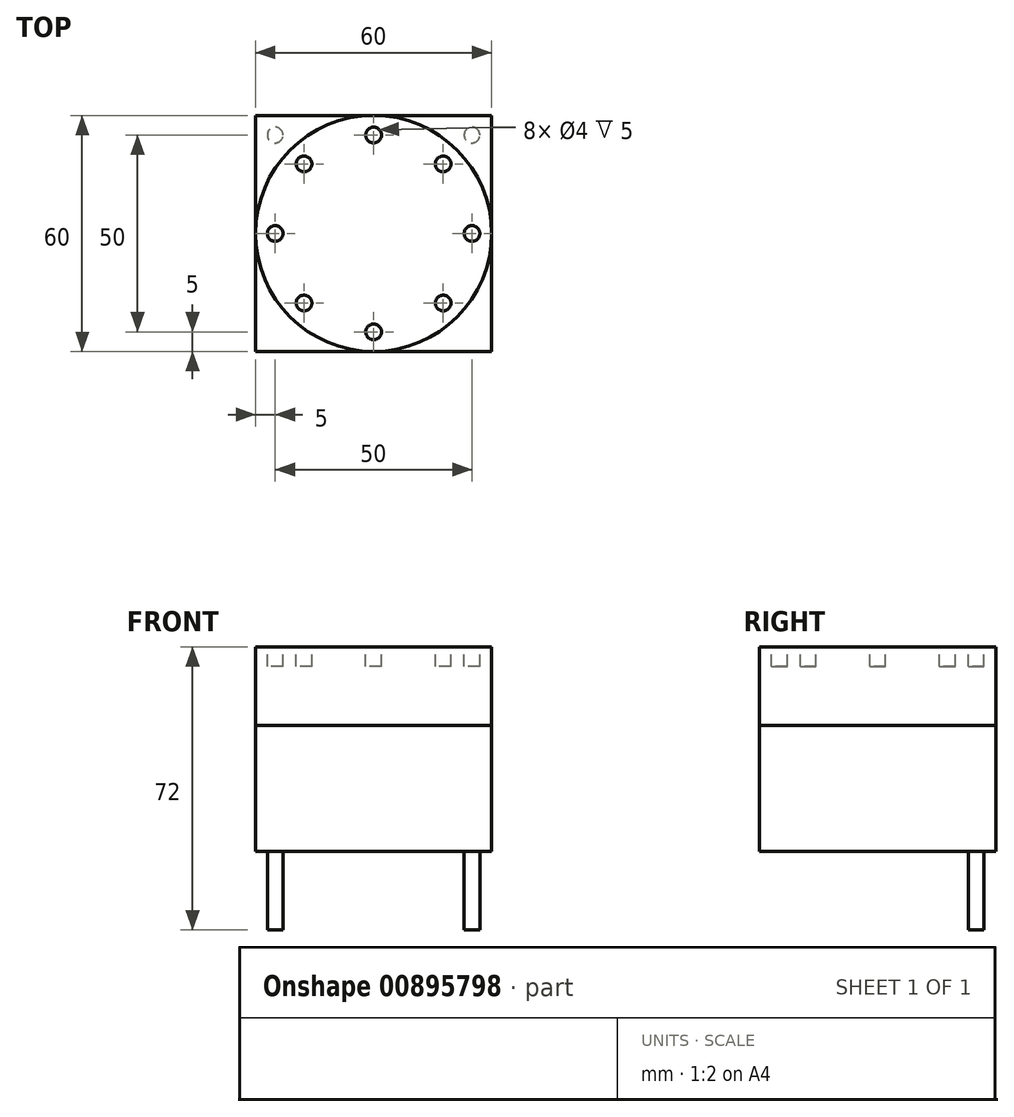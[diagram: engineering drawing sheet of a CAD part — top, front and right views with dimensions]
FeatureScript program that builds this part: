
annotation { "Feature Type Name" : "Feature", "Feature Type Description" : "" }
export const myFeature = defineFeature(function(context is Context, id is Id, definition is map)
    precondition{}
    {
        {
            var Q0;
            Q0=qCreatedBy(makeId("Top.planeOp"),FACE);
            var sketch = newSketch(context, id + "F0", { "sketchPlane" : qUnion([Q0])});
            skLineSegment(sketch, "E0.bottom", {"start": v(-30, 30) * mm, "end": v(30, 30) * mm});
            skLineSegment(sketch, "E0.top", {"start": v(-30, -30) * mm, "end": v(30, -30) * mm});
            skLineSegment(sketch, "E0.left", {"start": v(-30, 30) * mm, "end": v(-30, -30) * mm});
            skLineSegment(sketch, "E0.right", {"start": v(30, 30) * mm, "end": v(30, -30) * mm});
            skPoint(sketch, "E0.middle", {"position": v(0, 0) * mm});
            skCircle(sketch, "E1", {"center": v(0, 0) * mm, "radius": 30 * mm});
            skSolve(sketch);
        }
        {
            var Q0;
            Q0 = qSketchRegion(id + "F0", true);
            extrude(context, id + "F1", {"entities" : qUnion([Q0]), "oppositeDirection" : true, "depth" : 52 * mm, "offsetDistance" : 25 * mm});
        }
        {
            var Q0;
            {var subQ0=sQuery(id+"F0.wireOp",EDGE,"E1");var subQ1=makeQuery(id+"F0.imprint","INTERSECT",VERTEX,{"derivedFrom":[sQuery(id+"F0.wireOp",EDGE,"E0.bottom"),subQ0]});Q0=makeQuery(id+"F0.imprint","IMPRINT",FACE,{"disambiguationData":[TD([[makeQuery(id+"F0.imprint","IMPRINT",EDGE,{"disambiguationData":[TD([[subQ1,1.0]])],"derivedFrom":subQ0}),1.0]])]});}
            extrude(context, id + "F2", {"entities" : qUnion([Q0]), "operationType" : NewBodyOperationType.ADD, "depth" : 20 * mm, "offsetDistance" : 25 * mm});
        }
        {
            var Q0;
            Q0=makeQuery(id+"F2.opExtrude","CAP_FACE",FACE,{"disambiguationData":[OSD([sQuery(id+"F0.wireOp",EDGE,"E1")])],"isStart":false});
            var sketch = newSketch(context, id + "F3", { "sketchPlane" : qUnion([Q0])});
            skCircle(sketch, "E2", {"center": v(0, 25) * mm, "radius": 2 * mm});
            skCircle(sketch, "E3.1.0", {"center": v(-17.68, 17.68) * mm, "radius": 2 * mm});
            skCircle(sketch, "E3.2.0", {"center": v(-25, 0) * mm, "radius": 2 * mm});
            skCircle(sketch, "E3.3.0", {"center": v(-17.68, -17.68) * mm, "radius": 2 * mm});
            skCircle(sketch, "E3.4.0", {"center": v(0, -25) * mm, "radius": 2 * mm});
            skCircle(sketch, "E3.5.0", {"center": v(17.68, -17.68) * mm, "radius": 2 * mm});
            skCircle(sketch, "E3.6.0", {"center": v(25, 0) * mm, "radius": 2 * mm});
            skCircle(sketch, "E3.7.0", {"center": v(17.68, 17.68) * mm, "radius": 2 * mm});
            skPoint(sketch, "E3.center", {"position": v(0, 0) * mm});
            skSolve(sketch);
        }
        {
            var Q0;
            Q0 = qSketchRegion(id + "F3", true);
            extrude(context, id + "F4", {"entities" : qUnion([Q0]), "operationType" : NewBodyOperationType.REMOVE, "oppositeDirection" : true, "depth" : 5 * mm, "offsetDistance" : 25 * mm});
        }
        {
            var Q0;
            Q0=makeQuery(id+"F1.opExtrude","CAP_FACE",FACE,{"disambiguationData":[OSD([sQuery(id+"F0.wireOp",EDGE,"E0.bottom"),sQuery(id+"F0.wireOp",EDGE,"E0.top"),sQuery(id+"F0.wireOp",EDGE,"E0.left"),sQuery(id+"F0.wireOp",EDGE,"E0.right")])],"isStart":false});
            var sketch = newSketch(context, id + "F5", { "sketchPlane" : qUnion([Q0])});
            skCircle(sketch, "E4", {"center": v(-25, 25) * mm, "radius": 2 * mm});
            skCircle(sketch, "E5", {"center": v(25, 25) * mm, "radius": 2 * mm});
            skCircle(sketch, "E6.MirrorC", {"center": v(25, -25) * mm, "radius": 2 * mm});
            skCircle(sketch, "E7.MirrorC", {"center": v(-25, -25) * mm, "radius": 2 * mm});
            skSolve(sketch);
        }
        {
            var Q0;
            Q0=makeQuery(id+"F5.imprint","IMPRINT",FACE,{"disambiguationData":[TD([[makeQuery(id+"F5.imprint","IMPRINT",EDGE,{"derivedFrom":sQuery(id+"F5.wireOp",EDGE,"E4")}),1.0]])]});
            var Q1;
            Q1=makeQuery(id+"F5.imprint","IMPRINT",FACE,{"disambiguationData":[TD([[makeQuery(id+"F5.imprint","IMPRINT",EDGE,{"derivedFrom":sQuery(id+"F5.wireOp",EDGE,"E6.MirrorC")}),-1.0]])]});
            var Q2;
            Q2=makeQuery(id+"F5.imprint","IMPRINT",FACE,{"disambiguationData":[TD([[makeQuery(id+"F5.imprint","IMPRINT",EDGE,{"derivedFrom":sQuery(id+"F5.wireOp",EDGE,"E5")}),1.0]])]});
            var Q3;
            Q3=makeQuery(id+"F5.imprint","IMPRINT",FACE,{"disambiguationData":[TD([[makeQuery(id+"F5.imprint","IMPRINT",EDGE,{"derivedFrom":sQuery(id+"F5.wireOp",EDGE,"E7.MirrorC")}),-1.0]])]});
            extrude(context, id + "F6", {"entities" : qUnion([Q0, Q1, Q2, Q3]), "operationType" : NewBodyOperationType.REMOVE, "oppositeDirection" : true, "depth" : 20 * mm, "offsetDistance" : 25 * mm});
        }
    });
